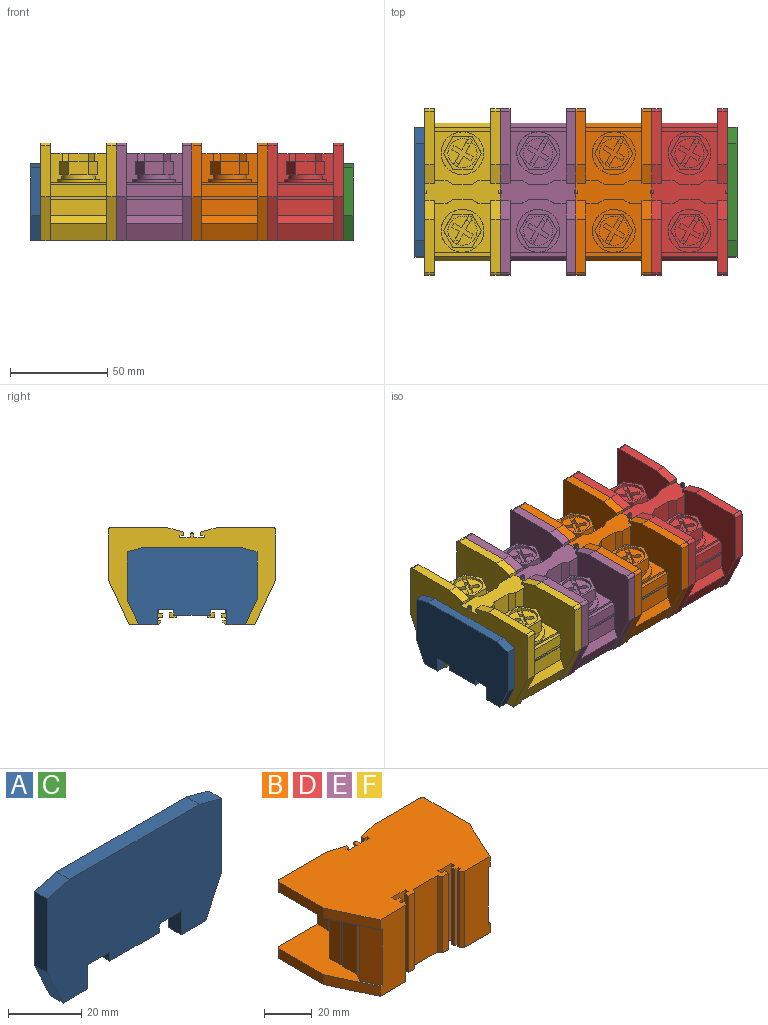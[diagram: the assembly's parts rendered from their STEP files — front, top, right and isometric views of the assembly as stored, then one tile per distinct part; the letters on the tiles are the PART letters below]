
ASSEMBLY  parts=6 mates=10
PART A: 18 faces, bbox 67x5x40 mm
  f0: plane 19x5mm, normal (0,0,-1), area 95mm2, adj f1,f9,f11,f17
  f1: plane 5x3mm, normal (1,0,0), area 15mm2, adj f0,f2,f9,f17
  f2: plane 8.5x5mm, normal (0,0,-1), area 42.5mm2, adj f1,f3,f9,f17
  f3: plane 8x5mm, normal (-1,0,0), area 40mm2, adj f2,f4,f9,f17
  f4: plane 9.44x5mm, normal (0,0,-1), area 47.2mm2, adj f3,f5,f9,f17
  f5: plane 13x6.06mm, normal (0.91,0,-0.42), area 71.7mm2, adj f4,f6,f9,f17
  f6: plane 24.72x5mm, normal (1,0,0), area 123.6mm2, adj f5,f7,f9,f17
  f7: plane 8.5x5mm, normal (0.26,0,0.97), area 44mm2, adj f6,f8,f9,f17
  f8: plane 50x5mm, normal (0,0,1), area 250mm2, adj f7,f9,f10,f17
  f9: plane 67x40mm, normal (0,-1,0), area 2350.8mm2, adj f0,f1,f2,f3,f4,f5,f6,f7
  f10: plane 8.5x5mm, normal (-0.26,0,0.97), area 44mm2, adj f8,f9,f16,f17
  f11: plane 5x3mm, normal (-1,0,0), area 15mm2, adj f0,f9,f12,f17
  f12: plane 8.5x5mm, normal (0,0,-1), area 42.5mm2, adj f9,f11,f13,f17
  f13: plane 8x5mm, normal (1,0,0), area 40mm2, adj f9,f12,f14,f17
  f14: plane 9.44x5mm, normal (0,0,-1), area 47.2mm2, adj f9,f13,f15,f17
  f15: plane 13x6.06mm, normal (-0.91,0,-0.42), area 71.7mm2, adj f9,f14,f16,f17
  f16: plane 24.72x5mm, normal (-1,0,0), area 123.6mm2, adj f9,f10,f15,f17
  f17: plane 67x40mm, normal (0,1,0), area 2350.8mm2, adj f0,f1,f2,f3,f4,f5,f6,f7
PART B: 190 faces, bbox 86x50.5x39 mm
  f0: plane 50.5x38.5mm, normal (0,0,1), area 924.2mm2, adj f1,f2,f3,f4,f5,f6,f7,f8
  f1: plane 22.8x10.63mm, normal (0.91,-0.42,0), area 125.8mm2, adj f0,f2,f36,f160
  f2: plane 26.2x5mm, normal (1,0,0), area 131mm2, adj f0,f1,f3,f36
  f3: cylinder r=1.5mm len=5mm, axis (0,0,1), area 11.8mm2, adj f0,f2,f4,f36
  f4: plane 27.5x5mm, normal (0,1,0), area 137.5mm2, adj f0,f3,f5,f36
  f5: plane 9.5x5mm, normal (-0.26,0.96,0), area 49.2mm2, adj f0,f4,f6,f36
  f6: plane 5x1.6mm, normal (-1,0,0), area 8mm2, adj f0,f5,f7,f36
  f7: plane 5x1.75mm, normal (0,-1,0), area 8.8mm2, adj f0,f6,f8,f36
  f8: plane 5x1.3mm, normal (-1,0,0), area 6.5mm2, adj f0,f7,f9,f36
  f9: plane 39x12.5mm, normal (0,1,0), area 415.9mm2, adj f0,f8,f10,f12,f13,f14,f15,f16
  f10: plane 15x6.04mm, normal (1,0,0), area 90.5mm2, adj f0,f9,f11,f14
  f11: plane 29x27mm, normal (0,1,0), area 371.8mm2, adj f0,f10,f12,f13,f14,f15,f16,f35
  f12: plane 15x3.46mm, normal (0.87,0,-0.5), area 60mm2, adj f9,f11,f13,f15
  f13: plane 15x10mm, normal (1,0,0), area 150mm2, adj f9,f11,f12,f14
  f14: plane 15x3.46mm, normal (0.87,0,0.5), area 60mm2, adj f9,f10,f11,f13
  f15: plane 15x6.04mm, normal (1,0,0), area 90.5mm2, adj f9,f11,f12,f16
  f16: plane 50.5x38.5mm, normal (0,0,-1), area 924.2mm2, adj f9,f11,f15,f17,f18,f19,f20,f21
  f17: plane 26.2x5mm, normal (1,0,0), area 131mm2, adj f16,f18,f24,f25
  f18: cylinder r=1.5mm len=5mm, axis (0,0,-1), area 11.8mm2, adj f16,f17,f19,f24
  f19: plane 27.5x5mm, normal (0,1,0), area 137.5mm2, adj f16,f18,f20,f24
  f20: plane 9.5x5mm, normal (-0.26,0.96,0), area 49.2mm2, adj f16,f19,f21,f24
  f21: plane 5x1.6mm, normal (-1,0,0), area 8mm2, adj f16,f20,f22,f24
  f22: plane 5x1.75mm, normal (0,-1,0), area 8.8mm2, adj f16,f21,f23,f24
  f23: plane 5x1.3mm, normal (-1,0,0), area 6.5mm2, adj f9,f16,f22,f24
  f24: plane 86x50.5mm, normal (0,0,1), area 3821.3mm2, adj f9,f17,f18,f19,f20,f21,f22,f23
  f25: plane 22.8x10.63mm, normal (0.91,-0.42,0), area 125.8mm2, adj f16,f17,f24,f160
  f26: plane 39x15.17mm, normal (0,-1,0), area 560.7mm2, adj f24,f36,f42,f44,f55,f63,f64,f161
  f27: plane 29x9mm, normal (0.91,-0.42,0), area 288mm2, adj f0,f16,f28,f160
  f28: plane 29x4.33mm, normal (0.87,0.5,0), area 145mm2, adj f0,f16,f27,f29
  f29: plane 29x8.17mm, normal (1,0,0), area 236.9mm2, adj f0,f16,f28,f30
  f30: plane 29x0.5mm, normal (0,1,0), area 14.5mm2, adj f0,f16,f29,f31
  f31: plane 29x1.5mm, normal (1,0,0), area 43.5mm2, adj f0,f16,f30,f32
  f32: plane 29x0.5mm, normal (0,-1,0), area 14.5mm2, adj f0,f16,f31,f33
  f33: plane 29x6mm, normal (1,0,0), area 174mm2, adj f0,f16,f32,f34
  f34: plane 29x2mm, normal (0,1,0), area 58mm2, adj f0,f16,f33,f35
  f35: plane 29x1mm, normal (1,0,0), area 29mm2, adj f0,f11,f16,f34
  f36: plane 86x50.5mm, normal (0,0,-1), area 3821.3mm2, adj f1,f2,f3,f4,f5,f6,f7,f8
  f37: plane 1.5x0.8mm, normal (1,0,0), area 1.2mm2, adj f9,f36,f38,f40
  f38: plane 2.5x2mm, normal (0,0,1), area 4.6mm2, adj f9,f37,f39,f40
  f39: plane 1.5x0.8mm, normal (-1,0,0), area 1.2mm2, adj f9,f36,f38,f40
  f40: cylinder r=1mm len=2mm, axis (0,0,-1), area 2.5mm2, adj f36,f37,f38,f39
  f41: plane 5x1.3mm, normal (1,0,0), area 6.5mm2, adj f9,f36,f42,f49
  f42: plane 50.5x38.5mm, normal (0,0,1), area 924.2mm2, adj f9,f26,f41,f43,f44,f45,f46,f47
  f43: plane 26.2x5mm, normal (-1,0,0), area 131mm2, adj f36,f42,f44,f45
  f44: plane 22.8x10.63mm, normal (-0.91,-0.42,0), area 125.8mm2, adj f26,f36,f42,f43
  f45: cylinder r=1.5mm len=5mm, axis (0,0,1), area 11.8mm2, adj f36,f42,f43,f46
  f46: plane 27.5x5mm, normal (0,1,0), area 137.5mm2, adj f36,f42,f45,f47
  f47: plane 9.5x5mm, normal (0.26,0.96,0), area 49.2mm2, adj f36,f42,f46,f48
  f48: plane 5x1.6mm, normal (1,0,0), area 8mm2, adj f36,f42,f47,f49
  f49: plane 5x1.75mm, normal (0,-1,0), area 8.8mm2, adj f36,f41,f42,f48
  f50: plane 15x6.04mm, normal (-1,0,0), area 90.5mm2, adj f9,f42,f51,f73
  f51: plane 15x3.46mm, normal (-0.87,0,0.5), area 60mm2, adj f9,f50,f52,f73
  f52: plane 15x10mm, normal (-1,0,0), area 150mm2, adj f9,f51,f53,f73
  f53: plane 15x3.46mm, normal (-0.87,0,-0.5), area 60mm2, adj f9,f52,f54,f73
  f54: plane 15x6.04mm, normal (-1,0,0), area 90.5mm2, adj f9,f53,f55,f73
  f55: plane 50.5x38.5mm, normal (0,0,-1), area 924.2mm2, adj f9,f26,f54,f56,f57,f58,f59,f60
  f56: plane 5x1.3mm, normal (1,0,0), area 6.5mm2, adj f9,f24,f55,f57
  f57: plane 5x1.75mm, normal (0,-1,0), area 8.8mm2, adj f24,f55,f56,f58
  f58: plane 5x1.6mm, normal (1,0,0), area 8mm2, adj f24,f55,f57,f59
  f59: plane 9.5x5mm, normal (0.26,0.96,0), area 49.2mm2, adj f24,f55,f58,f60
  f60: plane 27.5x5mm, normal (0,1,0), area 137.5mm2, adj f24,f55,f59,f61
  f61: cylinder r=1.5mm len=5mm, axis (0,0,-1), area 11.8mm2, adj f24,f55,f60,f62
  f62: plane 26.2x5mm, normal (-1,0,0), area 131mm2, adj f24,f55,f61,f63
  f63: plane 22.8x10.63mm, normal (-0.91,-0.42,0), area 125.8mm2, adj f24,f26,f55,f62
  f64: plane 29x9mm, normal (-0.91,-0.42,0), area 288mm2, adj f26,f42,f55,f65
  f65: plane 29x4.33mm, normal (-0.87,0.5,0), area 145mm2, adj f42,f55,f64,f66
  f66: plane 29x8.17mm, normal (-1,0,0), area 236.9mm2, adj f42,f55,f65,f67
  f67: plane 29x0.5mm, normal (0,1,0), area 14.5mm2, adj f42,f55,f66,f68
  f68: plane 29x1.5mm, normal (-1,0,0), area 43.5mm2, adj f42,f55,f67,f69
  f69: plane 29x0.5mm, normal (0,-1,0), area 14.5mm2, adj f42,f55,f68,f70
  f70: plane 29x6mm, normal (-1,0,0), area 174mm2, adj f42,f55,f69,f71
  f71: plane 29x2mm, normal (0,1,0), area 58mm2, adj f42,f55,f70,f72
  f72: plane 29x1mm, normal (-1,0,0), area 29mm2, adj f42,f55,f71,f73
  f73: plane 29x27mm, normal (0,1,0), area 371.8mm2, adj f42,f50,f51,f52,f53,f54,f55,f72
  f74: cylinder r=11mm len=22mm, axis (0,1,0), area 110.6mm2, adj f73,f76
  f75: plane 2.78x1.6mm, normal (0,1,0), area 0.3mm2, adj f124,f133
  f76: plane 22x22mm, normal (0,1,0), area 145.1mm2, adj f74,f77
  f77: cylinder r=8.65mm len=17.3mm, axis (0,1,0), area 135.9mm2, adj f76,f79,f81,f83,f85,f87,f89,f111
  f78: plane 3.21x0.15mm, normal (0,1,0), area 0.3mm2, adj f124,f129
  f79: plane 5.72x1.65mm, normal (0,-1,0), area 2.9mm2, adj f77,f80,f90
  f80: plane 8.5x7mm, normal (0.5,0,-0.87), area 68.7mm2, adj f79,f81,f82,f90,f91,f116
  f81: plane 4.96x2.86mm, normal (0,-1,0), area 2.9mm2, adj f77,f80,f82
  f82: plane 9.82x7mm, normal (1,0,0), area 68.7mm2, adj f80,f81,f83,f84,f91,f115
  f83: plane 4.96x2.86mm, normal (0,-1,0), area 2.9mm2, adj f77,f82,f84
  f84: plane 8.5x7mm, normal (0.5,0,0.87), area 68.7mm2, adj f82,f83,f85,f86,f91,f114
  f85: plane 5.72x1.65mm, normal (0,-1,0), area 2.9mm2, adj f77,f84,f86
  f86: plane 8.5x7mm, normal (-0.5,0,0.87), area 68.7mm2, adj f84,f85,f87,f88,f91,f113
  f87: plane 4.96x2.86mm, normal (0,-1,0), area 2.9mm2, adj f77,f86,f88
  f88: plane 9.82x7mm, normal (-1,0,0), area 68.7mm2, adj f86,f87,f89,f90,f91,f112
  f89: plane 4.96x2.86mm, normal (0,-1,0), area 2.9mm2, adj f77,f88,f90
  f90: plane 8.5x7mm, normal (-0.5,0,-0.87), area 68.7mm2, adj f79,f80,f88,f89,f91,f111
  f91: plane 19.63x17mm, normal (0,1,0), area 71.2mm2, adj f80,f82,f84,f86,f88,f90,f92,f93
  f92: cylinder r=7.5mm len=15mm, axis (0,1,0), area 65mm2, adj f91,f93,f94,f99,f101,f102,f106,f110
  f93: plane 6.31x4mm, normal (-0.5,0,0.87), area 16.1mm2, adj f91,f92,f94,f95,f96,f107,f108,f109
  f94: plane 13.34x10.21mm, normal (0,1,0), area 60.6mm2, adj f92,f93,f95,f97,f98,f99
  f95: plane 3.98x2.6mm, normal (-0.87,0,-0.5), area 12mm2, adj f93,f94,f96,f98
  f96: plane 11.11x11.11mm, normal (0,1,0), area 47.6mm2, adj f93,f95,f97,f98,f99,f100,f101,f103
  f97: plane 3.98x2.6mm, normal (0.87,0,0.5), area 12mm2, adj f94,f96,f98,f99
  f98: plane 2.6x1.99mm, normal (-0.5,0,0.87), area 6mm2, adj f94,f95,f96,f97
  f99: plane 5.42x3.13mm, normal (-0.5,0,0.87), area 13.6mm2, adj f92,f94,f96,f97,f100,f110
  f100: plane 1.99x1.6mm, normal (0.87,0,0.5), area 3.7mm2, adj f96,f99,f101,f110
  f101: plane 5.42x3.13mm, normal (0.5,0,-0.87), area 13.6mm2, adj f92,f96,f100,f102,f103,f110
  f102: plane 13.34x10.21mm, normal (0,1,0), area 60.6mm2, adj f92,f101,f103,f104,f105,f106
  f103: plane 3.98x2.6mm, normal (0.87,0,0.5), area 12mm2, adj f96,f101,f102,f104
  f104: plane 2.6x1.99mm, normal (0.5,0,-0.87), area 6mm2, adj f96,f102,f103,f105
  f105: plane 3.98x2.6mm, normal (-0.87,0,-0.5), area 12mm2, adj f96,f102,f104,f106
  f106: plane 6.31x4mm, normal (0.5,0,-0.87), area 16.1mm2, adj f91,f92,f96,f102,f105,f107,f108,f109
  f107: plane 1.99x1.6mm, normal (-0.87,0,-0.5), area 3.7mm2, adj f93,f96,f106,f108
  f108: plane 3.48x3.34mm, normal (0,1,0), area 6.3mm2, adj f93,f106,f107,f109
  f109: cylinder r=8.52mm len=2.4mm, axis (0,1,0), area 5.5mm2, adj f91,f93,f106,f108
  f110: plane 2.82x2.59mm, normal (0,1,0), area 4mm2, adj f92,f99,f100,f101
  f111: plane 2.78x1.6mm, normal (0,1,0), area 0.3mm2, adj f77,f90
  f112: plane 3.21x0.15mm, normal (0,1,0), area 0.3mm2, adj f77,f88
  f113: plane 2.78x1.6mm, normal (0,1,0), area 0.3mm2, adj f77,f86
  f114: plane 2.78x1.6mm, normal (0,1,0), area 0.3mm2, adj f77,f84
  f115: plane 3.21x0.15mm, normal (0,1,0), area 0.3mm2, adj f77,f82
  f116: plane 2.78x1.6mm, normal (0,1,0), area 0.3mm2, adj f77,f80
  f117: plane 1.5x0.8mm, normal (-1,0,0), area 1.2mm2, adj f9,f24,f118,f120
  f118: plane 2.5x2mm, normal (0,0,-1), area 4.6mm2, adj f9,f117,f119,f120
  f119: plane 1.5x0.8mm, normal (1,0,0), area 1.2mm2, adj f9,f24,f118,f120
  f120: cylinder r=1mm len=2mm, axis (0,0,1), area 2.5mm2, adj f24,f117,f118,f119
  f121: cylinder r=11mm len=22mm, axis (0,1,0), area 110.6mm2, adj f11,f122
  f122: plane 22x22mm, normal (0,1,0), area 145.1mm2, adj f121,f124
  f123: plane 2.78x1.6mm, normal (0,1,0), area 0.3mm2, adj f124,f131
  f124: cylinder r=8.65mm len=17.3mm, axis (0,1,0), area 135.9mm2, adj f75,f78,f122,f123,f125,f126,f128,f130
  f125: plane 2.78x1.6mm, normal (0,1,0), area 0.3mm2, adj f124,f127
  f126: plane 5.72x1.65mm, normal (0,-1,0), area 2.9mm2, adj f124,f127,f137
  f127: plane 8.5x7mm, normal (0.5,0,-0.87), area 68.7mm2, adj f125,f126,f128,f129,f137,f138
  f128: plane 4.96x2.86mm, normal (0,-1,0), area 2.9mm2, adj f124,f127,f129
  f129: plane 9.82x7mm, normal (1,0,0), area 68.7mm2, adj f78,f127,f128,f130,f131,f138
  f130: plane 4.96x2.86mm, normal (0,-1,0), area 2.9mm2, adj f124,f129,f131
  f131: plane 8.5x7mm, normal (0.5,0,0.87), area 68.7mm2, adj f123,f129,f130,f132,f133,f138
  f132: plane 5.72x1.65mm, normal (0,-1,0), area 2.9mm2, adj f124,f131,f133
  f133: plane 8.5x7mm, normal (-0.5,0,0.87), area 68.7mm2, adj f75,f131,f132,f134,f135,f138
  f134: plane 4.96x2.86mm, normal (0,-1,0), area 2.9mm2, adj f124,f133,f135
  f135: plane 9.82x7mm, normal (-1,0,0), area 68.7mm2, adj f133,f134,f136,f137,f138,f159
  f136: plane 4.96x2.86mm, normal (0,-1,0), area 2.9mm2, adj f124,f135,f137
  f137: plane 8.5x7mm, normal (-0.5,0,-0.87), area 68.7mm2, adj f126,f127,f135,f136,f138,f158
  f138: plane 19.63x17mm, normal (0,1,0), area 71.2mm2, adj f127,f129,f131,f133,f135,f137,f139,f140
  f139: cylinder r=7.5mm len=15mm, axis (0,1,0), area 65mm2, adj f138,f140,f141,f146,f148,f149,f153,f157
  f140: plane 6.31x4mm, normal (-0.5,0,0.87), area 16.1mm2, adj f138,f139,f141,f142,f143,f154,f155,f156
  f141: plane 13.34x10.21mm, normal (0,1,0), area 60.6mm2, adj f139,f140,f142,f144,f145,f146
  f142: plane 3.98x2.6mm, normal (-0.87,0,-0.5), area 12mm2, adj f140,f141,f143,f145
  f143: plane 11.11x11.11mm, normal (0,1,0), area 47.6mm2, adj f140,f142,f144,f145,f146,f147,f148,f150
  f144: plane 3.98x2.6mm, normal (0.87,0,0.5), area 12mm2, adj f141,f143,f145,f146
  f145: plane 2.6x1.99mm, normal (-0.5,0,0.87), area 6mm2, adj f141,f142,f143,f144
  f146: plane 5.42x3.13mm, normal (-0.5,0,0.87), area 13.6mm2, adj f139,f141,f143,f144,f147,f157
  f147: plane 1.99x1.6mm, normal (0.87,0,0.5), area 3.7mm2, adj f143,f146,f148,f157
  f148: plane 5.42x3.13mm, normal (0.5,0,-0.87), area 13.6mm2, adj f139,f143,f147,f149,f150,f157
  f149: plane 13.34x10.21mm, normal (0,1,0), area 60.6mm2, adj f139,f148,f150,f151,f152,f153
  f150: plane 3.98x2.6mm, normal (0.87,0,0.5), area 12mm2, adj f143,f148,f149,f151
  f151: plane 2.6x1.99mm, normal (0.5,0,-0.87), area 6mm2, adj f143,f149,f150,f152
  f152: plane 3.98x2.6mm, normal (-0.87,0,-0.5), area 12mm2, adj f143,f149,f151,f153
  f153: plane 6.31x4mm, normal (0.5,0,-0.87), area 16.1mm2, adj f138,f139,f143,f149,f152,f154,f155,f156
  f154: plane 1.99x1.6mm, normal (-0.87,0,-0.5), area 3.7mm2, adj f140,f143,f153,f155
  f155: plane 3.48x3.34mm, normal (0,1,0), area 6.3mm2, adj f140,f153,f154,f156
  f156: cylinder r=8.52mm len=2.4mm, axis (0,1,0), area 5.5mm2, adj f138,f140,f153,f155
  f157: plane 2.82x2.59mm, normal (0,1,0), area 4mm2, adj f139,f146,f147,f148
  f158: plane 2.78x1.6mm, normal (0,1,0), area 0.3mm2, adj f124,f137
  f159: plane 3.21x0.15mm, normal (0,1,0), area 0.3mm2, adj f124,f135
  f160: plane 39x14.87mm, normal (0,-1,0), area 549mm2, adj f0,f1,f16,f24,f25,f27,f36,f189
  f161: plane 39x1.4mm, normal (0.71,-0.71,0), area 77.2mm2, adj f24,f26,f36,f162
  f162: plane 39x1mm, normal (1,0,0), area 39mm2, adj f24,f36,f161,f163
  f163: plane 39x1.5mm, normal (0,1,0), area 58.5mm2, adj f24,f36,f162,f164
  f164: plane 39x1.4mm, normal (1,0,0), area 54.6mm2, adj f24,f36,f163,f165
  f165: plane 39x2mm, normal (0,-1,0), area 78mm2, adj f24,f36,f164,f166
  f166: plane 39x2mm, normal (1,0,0), area 78mm2, adj f24,f36,f165,f167
  f167: plane 39x2.2mm, normal (0,1,0), area 85.8mm2, adj f24,f36,f166,f168
  f168: plane 39x2.2mm, normal (1,0,0), area 85.8mm2, adj f24,f36,f167,f169
  f169: plane 39x7.8mm, normal (0,-1,0), area 304.2mm2, adj f24,f36,f168,f170
  f170: plane 39x1.8mm, normal (-1,0,0), area 70.2mm2, adj f24,f36,f169,f171
  f171: plane 39x2.05mm, normal (0,1,0), area 79.9mm2, adj f24,f36,f170,f172
  f172: plane 39x2.4mm, normal (-1,0,0), area 93.6mm2, adj f24,f36,f171,f173
  f173: plane 39x3.6mm, normal (0,-1,0), area 140.2mm2, adj f24,f36,f172,f174
  f174: plane 39x2mm, normal (0.87,-0.5,0), area 90.1mm2, adj f24,f36,f173,f175
  f175: plane 39x14mm, normal (0,-1,0), area 546mm2, adj f24,f36,f174,f176
  f176: plane 39x2mm, normal (-0.87,-0.5,0), area 90.1mm2, adj f24,f36,f175,f177
  f177: plane 39x3.6mm, normal (0,-1,0), area 140.2mm2, adj f24,f36,f176,f178
  f178: plane 39x2.4mm, normal (1,0,0), area 93.6mm2, adj f24,f36,f177,f179
  f179: plane 39x2.05mm, normal (0,1,0), area 80mm2, adj f24,f36,f178,f180
  f180: plane 39x1.8mm, normal (1,0,0), area 70.2mm2, adj f24,f36,f179,f181
  f181: plane 39x7.8mm, normal (0,-1,0), area 304.2mm2, adj f24,f36,f180,f182
  f182: plane 39x2.2mm, normal (-1,0,0), area 85.8mm2, adj f24,f36,f181,f183
  f183: plane 39x2.2mm, normal (0,1,0), area 85.8mm2, adj f24,f36,f182,f184
  f184: plane 39x2mm, normal (-1,0,0), area 78mm2, adj f24,f36,f183,f185
  f185: plane 39x2.2mm, normal (0,-1,0), area 85.8mm2, adj f24,f36,f184,f186
  f186: plane 39x1.3mm, normal (-1,0,0), area 50.7mm2, adj f24,f36,f185,f187
  f187: plane 39x1.5mm, normal (0,1,0), area 58.5mm2, adj f24,f36,f186,f188
  f188: plane 39x1mm, normal (-1,0,0), area 39mm2, adj f24,f36,f187,f189
  f189: plane 39x1.5mm, normal (-0.71,-0.71,0), area 82.7mm2, adj f24,f36,f160,f188
PART C: same geometry as A
PART D: same geometry as B
PART E: same geometry as B
PART F: same geometry as B
PLACE A rot(axis=(0,0,1),90deg) t=(165.29,13.78,-2.91)mm
PLACE B rot(axis=(0.58,0.58,0.58),120deg) t=(253.29,59.71,26.56)mm
PLACE C rot(axis=(0,0,1),90deg) t=(326.29,13.78,-2.91)mm
PLACE D rot(axis=(0.58,0.58,0.58),120deg) t=(292.29,59.71,26.56)mm
PLACE E rot(axis=(0.58,0.58,0.58),120deg) t=(214.29,59.71,26.56)mm
PLACE F rot(axis=(0.58,0.58,0.58),120deg) t=(175.29,59.71,26.56)mm
MATE planar F.f26 <-> D.f26  axis (0,0,-1) through (189.79,-10.61,-2.91)mm
MATE planar E.f24 <-> B.f36  axis (1,0,0) through (248.29,13.78,24.17)mm
MATE planar A.f9 <-> F.f36  axis (1,0,0) through (170.29,13.78,19.09)mm
MATE planar C.f12 <-> D.f169  axis (0,0,-1) through (328.79,0.03,5.09)mm
MATE planar F.f26 <-> A.f14  axis (0,0,-1) through (189.79,-10.61,-2.91)mm
MATE planar F.f26 <-> E.f26  axis (0,0,-1) through (189.79,-10.61,-2.91)mm
MATE planar E.f36 <-> F.f24  axis (-1,0,0) through (209.29,13.78,24.17)mm
MATE planar C.f17 <-> D.f24  axis (-1,0,0) through (326.29,13.78,19.09)mm
MATE planar D.f36 <-> B.f24  axis (-1,0,0) through (287.29,13.78,24.17)mm
MATE planar F.f26 <-> B.f26  axis (0,0,-1) through (189.79,-10.61,-2.91)mm
